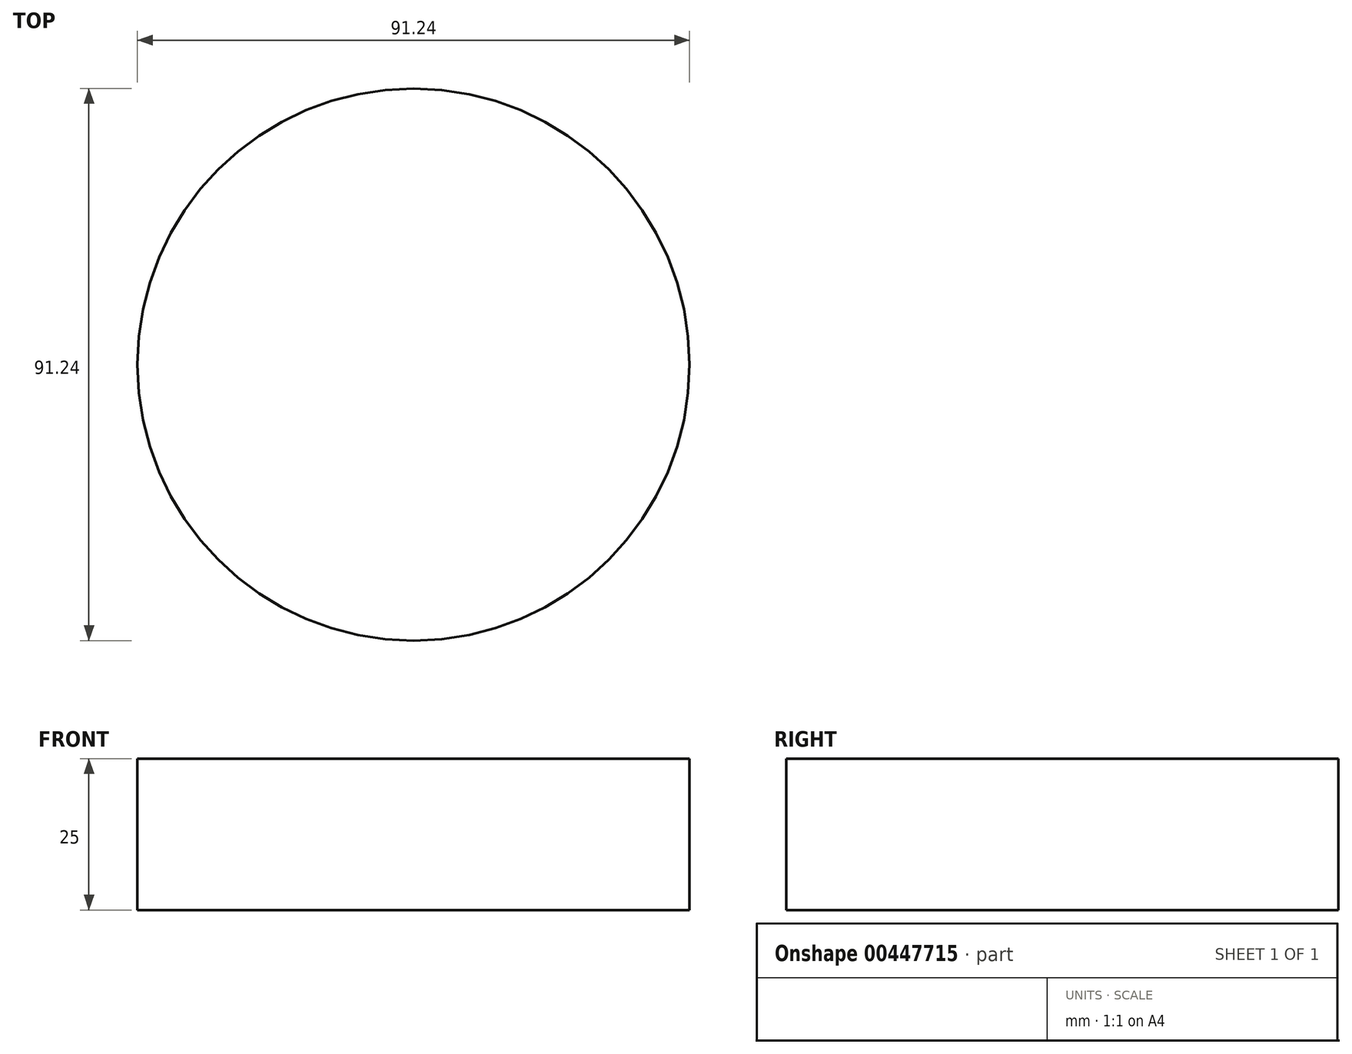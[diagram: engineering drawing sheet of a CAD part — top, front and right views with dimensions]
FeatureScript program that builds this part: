
annotation { "Feature Type Name" : "Feature", "Feature Type Description" : "" }
export const myFeature = defineFeature(function(context is Context, id is Id, definition is map)
    precondition{}
    {
        {
            var Q0;
            Q0=qCreatedBy(makeId("Top.planeOp"),FACE);
            var sketch = newSketch(context, id + "F0", { "sketchPlane" : qUnion([Q0])});
            skCircle(sketch, "E0", {"center": v(0, 0) * mm, "radius": 45.62 * mm});
            skSolve(sketch);
        }
        {
            var Q0;
            Q0=makeQuery(id+"F0.imprint","IMPRINT",FACE,{"disambiguationData":[TD([[makeQuery(id+"F0.imprint","IMPRINT",EDGE,{"derivedFrom":sQuery(id+"F0.wireOp",EDGE,"E0")}),1.0]])]});
            extrude(context, id + "F1", {"entities" : qUnion([Q0]), "depth" : 25 * mm, "offsetDistance" : 25 * mm});
        }
    });
